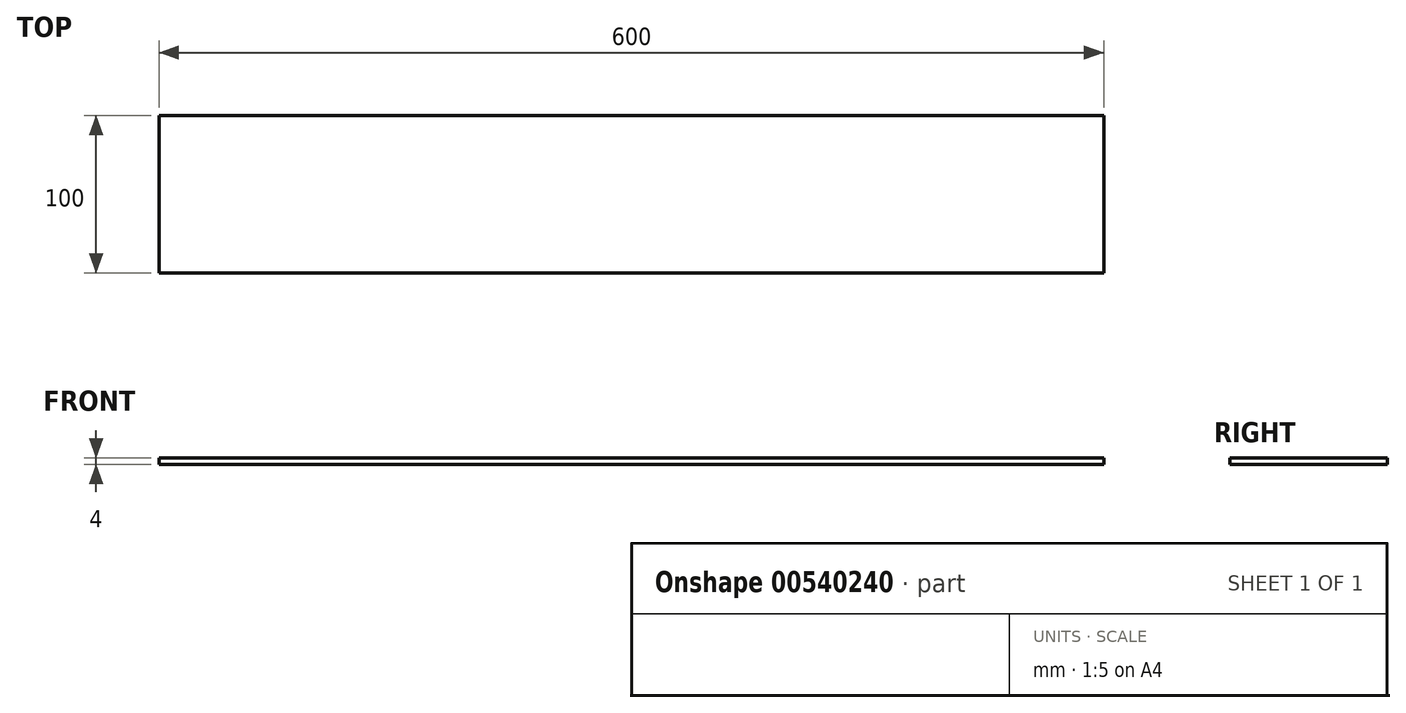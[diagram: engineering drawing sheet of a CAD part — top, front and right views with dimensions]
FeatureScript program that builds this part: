
annotation { "Feature Type Name" : "Feature", "Feature Type Description" : "" }
export const myFeature = defineFeature(function(context is Context, id is Id, definition is map)
    precondition{}
    {
        {
            var Q0;
            Q0=qCreatedBy(makeId("Top.planeOp"),FACE);
            var sketch = newSketch(context, id + "F0", { "sketchPlane" : qUnion([Q0])});
            skLineSegment(sketch, "E0.bottom", {"start": v(300, -50) * mm, "end": v(-300, -50) * mm});
            skLineSegment(sketch, "E0.top", {"start": v(300, 50) * mm, "end": v(-300, 50) * mm});
            skLineSegment(sketch, "E0.left", {"start": v(300, -50) * mm, "end": v(300, 50) * mm});
            skLineSegment(sketch, "E0.right", {"start": v(-300, -50) * mm, "end": v(-300, 50) * mm});
            skPoint(sketch, "E0.middle", {"position": v(0, 0) * mm});
            skSolve(sketch);
        }
        {
            var Q0;
            Q0=makeQuery(id+"F0.imprint","IMPRINT",FACE,{"disambiguationData":[TD([[makeQuery(id+"F0.imprint","IMPRINT",EDGE,{"derivedFrom":sQuery(id+"F0.wireOp",EDGE,"E0.bottom")}),-1.0]])]});
            extrude(context, id + "F1", {"entities" : qUnion([Q0]), "depth" : 4 * mm, "offsetDistance" : 25 * mm});
        }
    });
